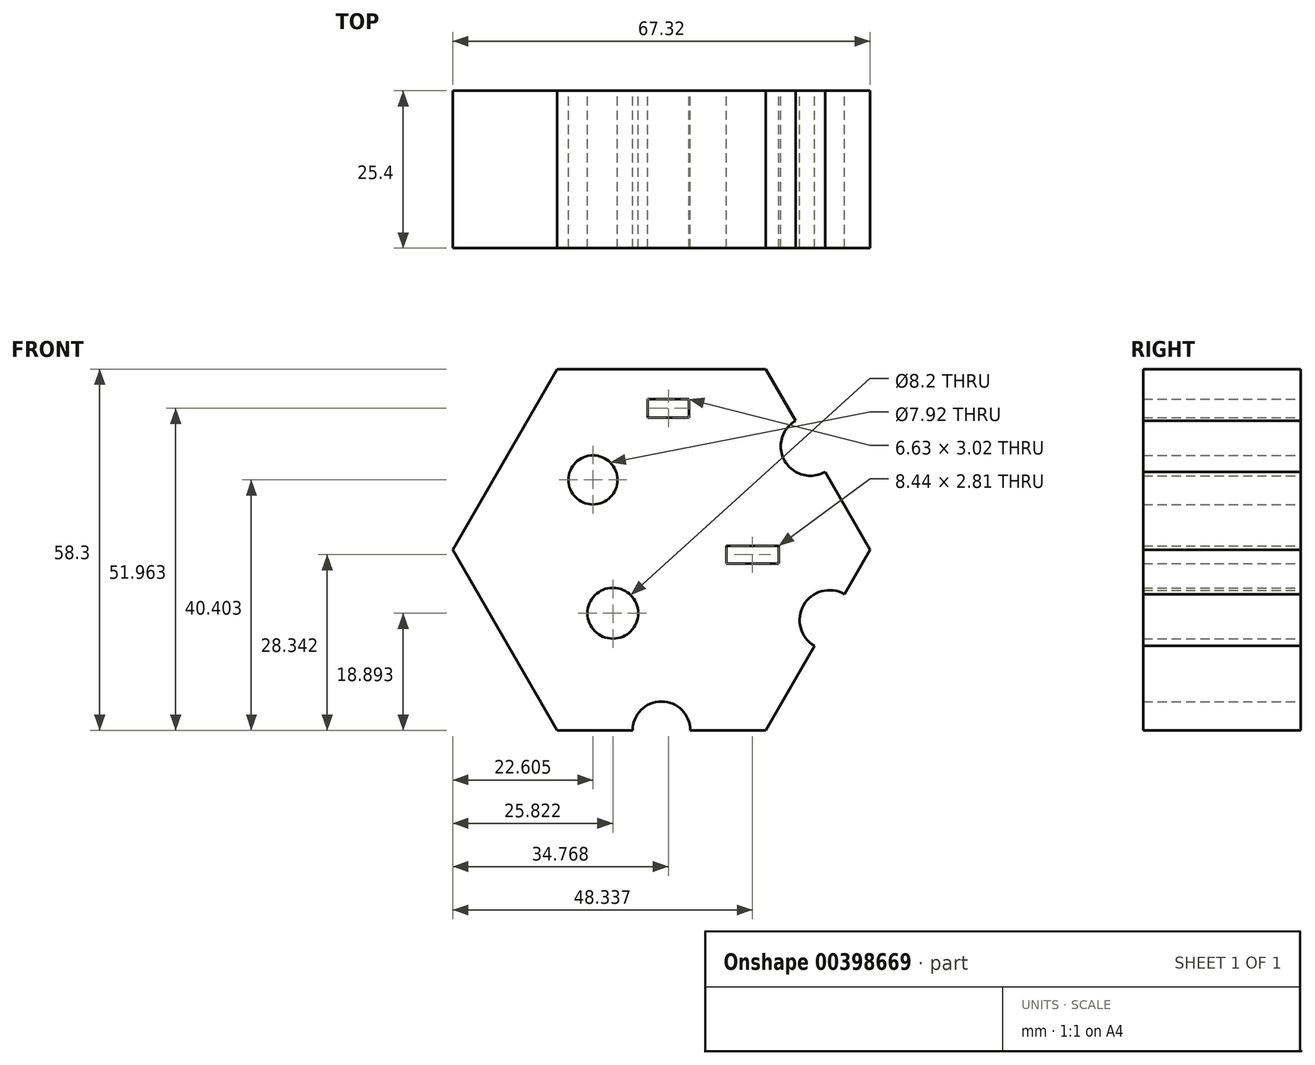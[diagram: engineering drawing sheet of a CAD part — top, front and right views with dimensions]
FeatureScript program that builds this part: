
annotation { "Feature Type Name" : "Feature", "Feature Type Description" : "" }
export const myFeature = defineFeature(function(context is Context, id is Id, definition is map)
    precondition{}
    {
        {
            var Q0;
            Q0=qCreatedBy(makeId("Front.planeOp"),FACE);
            var sketch = newSketch(context, id + "F0", { "sketchPlane" : qUnion([Q0])});
            skCircle(sketch, "E0.cCircle", {"center": v(-13.27, 24.53) * mm, "radius": 29.15 * mm, "construction": true});
            skLineSegment(sketch, "E0.0", {"start": v(3.56, -4.62) * mm, "end": v(-30.1, -4.62) * mm});
            skLineSegment(sketch, "E0.1", {"start": v(-30.1, -4.62) * mm, "end": v(-46.93, 24.53) * mm});
            skLineSegment(sketch, "E0.2", {"start": v(-46.93, 24.53) * mm, "end": v(-30.1, 53.68) * mm});
            skLineSegment(sketch, "E0.3", {"start": v(-30.1, 53.68) * mm, "end": v(3.56, 53.68) * mm});
            skLineSegment(sketch, "E0.4", {"start": v(3.56, 53.68) * mm, "end": v(20.4, 24.53) * mm});
            skLineSegment(sketch, "E0.5", {"start": v(20.4, 24.53) * mm, "end": v(3.56, -4.62) * mm});
            skPoint(sketch, "E0.0.midPoint", {"position": v(-13.27, -4.62) * mm});
            skCircle(sketch, "E1", {"center": v(-24.32, 35.78) * mm, "radius": 3.96 * mm});
            skCircle(sketch, "E2", {"center": v(-21.1, 14.27) * mm, "radius": 4.1 * mm});
            skCircle(sketch, "E3", {"center": v(10.76, 41.22) * mm, "radius": 4.77 * mm});
            skCircle(sketch, "E4", {"center": v(13.84, 13.17) * mm, "radius": 4.82 * mm});
            skCircle(sketch, "E5", {"center": v(-13.27, -4.62) * mm, "radius": 4.64 * mm});
            skLineSegment(sketch, "E6.bottom", {"start": v(-15.48, 48.85) * mm, "end": v(-8.85, 48.85) * mm});
            skLineSegment(sketch, "E6.top", {"start": v(-15.48, 45.83) * mm, "end": v(-8.85, 45.83) * mm});
            skLineSegment(sketch, "E6.left", {"start": v(-15.48, 48.85) * mm, "end": v(-15.48, 45.83) * mm});
            skLineSegment(sketch, "E6.right", {"start": v(-8.85, 48.85) * mm, "end": v(-8.85, 45.83) * mm});
            skLineSegment(sketch, "E7.bottom", {"start": v(-2.81, 25.13) * mm, "end": v(5.63, 25.13) * mm});
            skLineSegment(sketch, "E7.top", {"start": v(-2.81, 22.31) * mm, "end": v(5.63, 22.31) * mm});
            skLineSegment(sketch, "E7.left", {"start": v(-2.81, 25.13) * mm, "end": v(-2.81, 22.31) * mm});
            skLineSegment(sketch, "E7.right", {"start": v(5.63, 25.13) * mm, "end": v(5.63, 22.31) * mm});
            skSolve(sketch);
        }
        {
            var Q0;
            {var subQ14=sQuery(id+"F0.wireOp",EDGE,"E0.1");Q0=makeQuery(id+"F0.imprint","IMPRINT",FACE,{"disambiguationData":[TD([[makeQuery(id+"F0.imprint","IMPRINT",EDGE,{"derivedFrom":subQ14}),-1.0]])]});}
            var Q1;
            Q1=sQuery(id+"F0.wireOp",EDGE,"E0.3");
            extrude(context, id + "F1", {"entities" : qUnion([Q0]), "surfaceEntities" : qUnion([Q1]), "depth" : 25.4 * mm});
        }
    });
